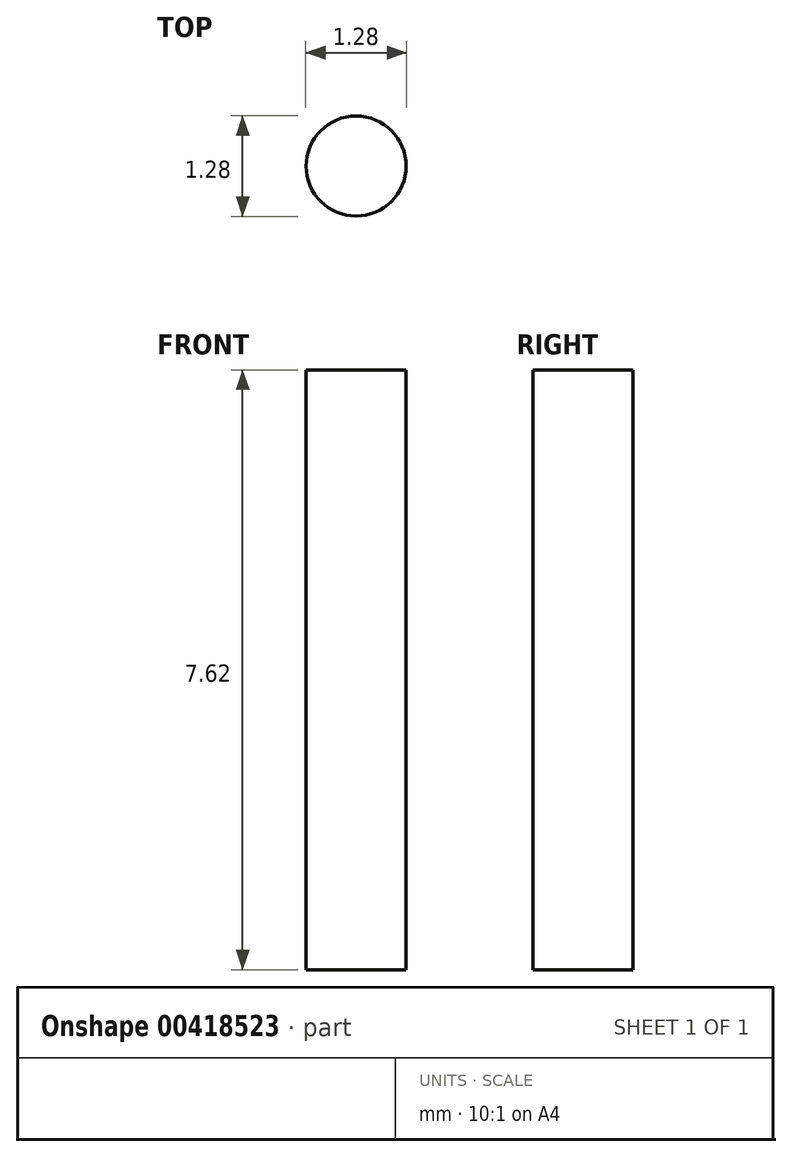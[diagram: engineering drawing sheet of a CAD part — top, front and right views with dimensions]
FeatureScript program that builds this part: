
annotation { "Feature Type Name" : "Feature", "Feature Type Description" : "" }
export const myFeature = defineFeature(function(context is Context, id is Id, definition is map)
    precondition{}
    {
        {
            var Q0;
            Q0=qCreatedBy(makeId("Top.planeOp"),FACE);
            var sketch = newSketch(context, id + "F0", { "sketchPlane" : qUnion([Q0])});
            skCircle(sketch, "E0", {"center": v(0, 0) * mm, "radius": 0.64 * mm});
            skSolve(sketch);
        }
        {
            var Q0;
            Q0=qCreatedBy(makeId("Front.planeOp"),FACE);
            var sketch = newSketch(context, id + "F1", { "sketchPlane" : qUnion([Q0])});
            skLineSegment(sketch, "E1", {"start": v(0, 0) * mm, "end": v(0, 7.62) * mm});
            skSolve(sketch);
        }
        {
            var Q0;
            Q0=makeQuery(id+"F0.imprint","IMPRINT",FACE,{"disambiguationData":[TD([[makeQuery(id+"F0.imprint","IMPRINT",EDGE,{"derivedFrom":sQuery(id+"F0.wireOp",EDGE,"E0")}),1.0]])]});
            var Q1;
            Q1=sQuery(id+"F1.wireOp",EDGE,"E1");
            sweep(context, id + "F2", {"profiles" : qUnion([Q0]), "path" : qUnion([Q1])});
        }
    });
